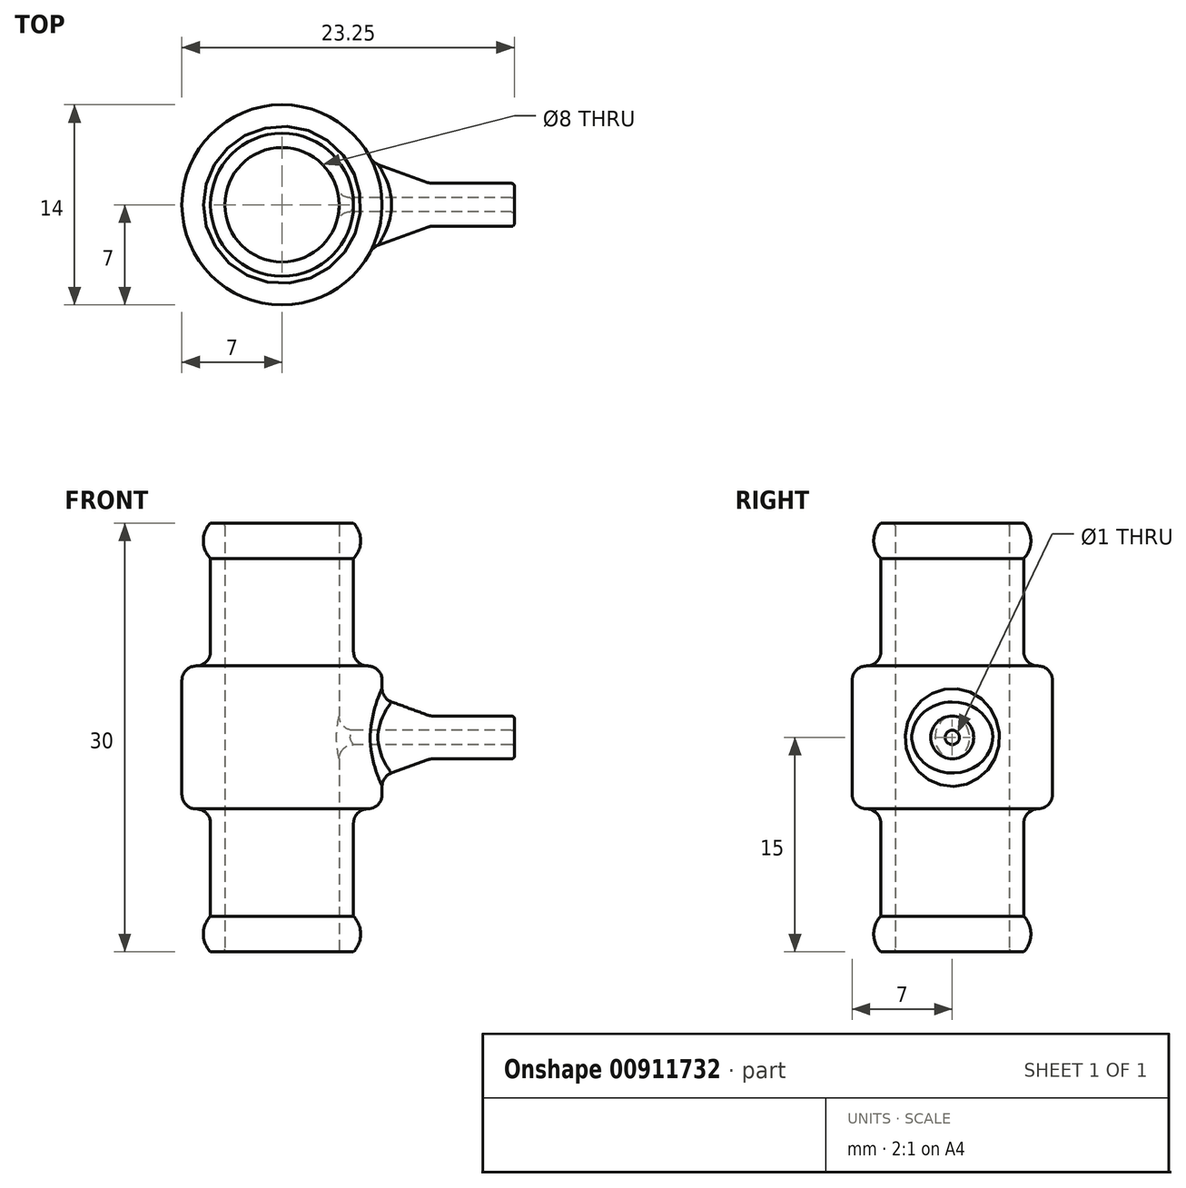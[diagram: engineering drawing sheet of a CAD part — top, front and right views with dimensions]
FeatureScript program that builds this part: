
annotation { "Feature Type Name" : "Feature", "Feature Type Description" : "" }
export const myFeature = defineFeature(function(context is Context, id is Id, definition is map)
    precondition{}
    {
        {
            var Q0;
            Q0=qCreatedBy(makeId("Right.planeOp"),FACE);
            var sketch = newSketch(context, id + "F0", { "sketchPlane" : qUnion([Q0])});
            skLineSegment(sketch, "E0", {"start": v(0, 0) * mm, "end": v(0, 12.47) * mm, "construction": true});
            skLineSegment(sketch, "E1", {"start": v(-4, 0) * mm, "end": v(-5, 0) * mm});
            skLineSegment(sketch, "E2", {"start": v(-5, 2.5) * mm, "end": v(-5, 10) * mm});
            skLineSegment(sketch, "E3", {"start": v(-5, 10) * mm, "end": v(-7, 10) * mm});
            skLineSegment(sketch, "E4", {"start": v(-7, 10) * mm, "end": v(-7, 20) * mm});
            skLineSegment(sketch, "E5", {"start": v(-7, 20) * mm, "end": v(-5, 20) * mm});
            skLineSegment(sketch, "E6", {"start": v(-5, 20) * mm, "end": v(-5, 27.5) * mm});
            skLineSegment(sketch, "E7", {"start": v(-5, 30) * mm, "end": v(-4, 30) * mm});
            skLineSegment(sketch, "E8", {"start": v(-4, 30) * mm, "end": v(-4, 0) * mm});
            skLineSegment(sketch, "E9", {"start": v(-5, 20) * mm, "end": v(-5, 4.37) * mm, "construction": true});
            skArc(sketch, "E10", {"start": v(-5, 30) * mm, "mid": v(-5.5, 28.75) * mm, "end": v(-5, 27.5) * mm});
            skArc(sketch, "E11", {"start": v(-5, 2.5) * mm, "mid": v(-5.5, 1.25) * mm, "end": v(-5, 0) * mm});
            skSolve(sketch);
        }
        {
            var Q0;
            Q0=makeQuery(id+"F0.imprint","IMPRINT",FACE,{"disambiguationData":[TD([[makeQuery(id+"F0.imprint","IMPRINT",EDGE,{"derivedFrom":sQuery(id+"F0.wireOp",EDGE,"E1")}),-1.0]])]});
            var Q1;
            Q1=sQuery(id+"F0.wireOp",EDGE,"E0");
            revolve(context, id + "F1", {"surfaceOperationType" : NewSurfaceOperationType.NEW, "entities" : qUnion([Q0]), "axis" : qUnion([Q1]), "revolveType" : RevolveType.FULL});
        }
        {
            var Q0;
            Q0=qCreatedBy(makeId("Front.planeOp"),FACE);
            var sketch = newSketch(context, id + "F2", { "sketchPlane" : qUnion([Q0])});
            skLineSegment(sketch, "E12", {"start": v(6.25, 15) * mm, "end": v(16.25, 15) * mm, "construction": true});
            skLineSegment(sketch, "E13.bottom", {"start": v(10.37, 13.5) * mm, "end": v(16.25, 13.5) * mm});
            skLineSegment(sketch, "E13.right", {"start": v(16.25, 13.5) * mm, "end": v(16.25, 14.5) * mm});
            skLineSegment(sketch, "E14", {"start": v(6.25, 14.5) * mm, "end": v(16.25, 14.5) * mm});
            skLineSegment(sketch, "E15", {"start": v(6.25, 12) * mm, "end": v(10.37, 13.5) * mm});
            skLineSegment(sketch, "E16.0", {"start": v(0, 20) * mm, "end": v(-7, 20) * mm, "construction": true});
            skLineSegment(sketch, "E17.trimOffspring", {"start": v(0.25, 10) * mm, "end": v(-7, 10) * mm, "construction": true});
            skLineSegment(sketch, "E18", {"start": v(6.25, 12) * mm, "end": v(6.25, 14.5) * mm});
            skLineSegment(sketch, "E19", {"start": v(0, 20) * mm, "end": v(6.25, 20) * mm, "construction": true});
            skLineSegment(sketch, "E20", {"start": v(6.25, 20) * mm, "end": v(6.25, 10) * mm, "construction": true});
            skLineSegment(sketch, "E21", {"start": v(6.25, 10) * mm, "end": v(0.25, 10) * mm, "construction": true});
            skSolve(sketch);
        }
        {
            var Q0;
            Q0 = qSketchRegion(id + "F2", true);
            var Q1;
            Q1=sQuery(id+"F2.wireOp",EDGE,"E12");
            revolve(context, id + "F3", {"operationType" : NewBodyOperationType.ADD, "surfaceOperationType" : NewSurfaceOperationType.NEW, "entities" : qUnion([Q0]), "axis" : qUnion([Q1]), "revolveType" : RevolveType.FULL});
        }
        {
            var Q0;
            Q0=makeQuery(id+"F3.opRevolve","SWEPT_FACE",FACE,{"disambiguationData":[OSD([sQuery(id+"F2.wireOp",EDGE,"E13.right")])]});
            var sketch = newSketch(context, id + "F4", { "sketchPlane" : qUnion([Q0])});
            skCircle(sketch, "E22.0", {"center": v(0, 15) * mm, "radius": 0.5 * mm});
            skSolve(sketch);
        }
        {
            var Q0;
            Q0 = qSketchRegion(id + "F4", true);
            extrude(context, id + "F5", {"entities" : qUnion([Q0]), "operationType" : NewBodyOperationType.REMOVE, "endBound" : BoundingType.SYMMETRIC, "oppositeDirection" : true, "depth" : 25 * mm, "offsetDistance" : 25 * mm});
        }
        {
            var Q0;
            Q0=makeQuery(id+"F1.opRevolve","SWEPT_EDGE",EDGE,{"disambiguationData":[OSD([sQuery(id+"F0.wireOp",EDGE,"E7"),sQuery(id+"F0.wireOp",EDGE,"E8")])]});
            var Q1;
            Q1=makeQuery(id+"F1.opRevolve","SWEPT_EDGE",EDGE,{"disambiguationData":[OSD([sQuery(id+"F0.wireOp",EDGE,"E1"),sQuery(id+"F0.wireOp",EDGE,"E8")])]});
            var Q2;
            Q2=makeQuery(id+"F3.opRevolve","SWEPT_EDGE",EDGE,{"disambiguationData":[OSD([sQuery(id+"F2.wireOp",EDGE,"E13.bottom"),sQuery(id+"F2.wireOp",EDGE,"E13.right")])]});
            var Q3;
            Q3=makeQuery(id+"F3.opRevolve","SWEPT_EDGE",EDGE,{"disambiguationData":[OSD([sQuery(id+"F2.wireOp",EDGE,"E13.right"),sQuery(id+"F2.wireOp",EDGE,"E14")])]});
            fillet(context, id + "F6", {"entities" : qUnion([Q0, Q1, Q2, Q3]), "radius" : 0.2 * mm, "tangentPropagation" : true, "allowEdgeOverflow" : false});
        }
        {
            var Q0;
            Q0=makeQuery(id+"F1.opRevolve","SWEPT_EDGE",EDGE,{"disambiguationData":[OSD([sQuery(id+"F0.wireOp",EDGE,"E3"),sQuery(id+"F0.wireOp",EDGE,"E4")])]});
            var Q1;
            Q1=makeQuery(id+"F1.opRevolve","SWEPT_EDGE",EDGE,{"disambiguationData":[OSD([sQuery(id+"F0.wireOp",EDGE,"E4"),sQuery(id+"F0.wireOp",EDGE,"E5")])]});
            var Q2;
            Q2=makeQuery(id+"F1.opRevolve","SWEPT_EDGE",EDGE,{"disambiguationData":[OSD([sQuery(id+"F0.wireOp",EDGE,"E5"),sQuery(id+"F0.wireOp",EDGE,"E6")])]});
            var Q3;
            Q3=makeQuery(id+"F1.opRevolve","SWEPT_EDGE",EDGE,{"disambiguationData":[OSD([sQuery(id+"F0.wireOp",EDGE,"E2"),sQuery(id+"F0.wireOp",EDGE,"E3")])]});
            var Q4;
            Q4=makeQuery(id+"F3.boolean.opBoolean","INTERSECT",EDGE,{"derivedFrom":[makeQuery(id+"F1.opRevolve","SWEPT_FACE",FACE,{"disambiguationData":[OSD([sQuery(id+"F0.wireOp",EDGE,"E4")])]}),makeQuery(id+"F3.opRevolve","SWEPT_FACE",FACE,{"disambiguationData":[OSD([sQuery(id+"F2.wireOp",EDGE,"E15")])]})]});
            var Q5;
            Q5=makeQuery(id+"F3.opRevolve","SWEPT_EDGE",EDGE,{"disambiguationData":[OSD([sQuery(id+"F2.wireOp",EDGE,"E13.bottom"),sQuery(id+"F2.wireOp",EDGE,"E15")])]});
            var Q6;
            Q6=makeQuery(id+"F5.boolean.opBoolean","INTERSECT",EDGE,{"derivedFrom":[makeQuery(id+"F1.opRevolve","SWEPT_FACE",FACE,{"disambiguationData":[OSD([sQuery(id+"F0.wireOp",EDGE,"E8")])]}),makeQuery(id+"F5.opExtrude","SWEPT_FACE",FACE,{"disambiguationData":[OSD([sQuery(id+"F4.wireOp",EDGE,"E22.0")])]})]});
            fillet(context, id + "F7", {"entities" : qUnion([Q0, Q1, Q2, Q3, Q4, Q5, Q6]), "radius" : 1 * mm, "tangentPropagation" : true, "allowEdgeOverflow" : false});
        }
    });
